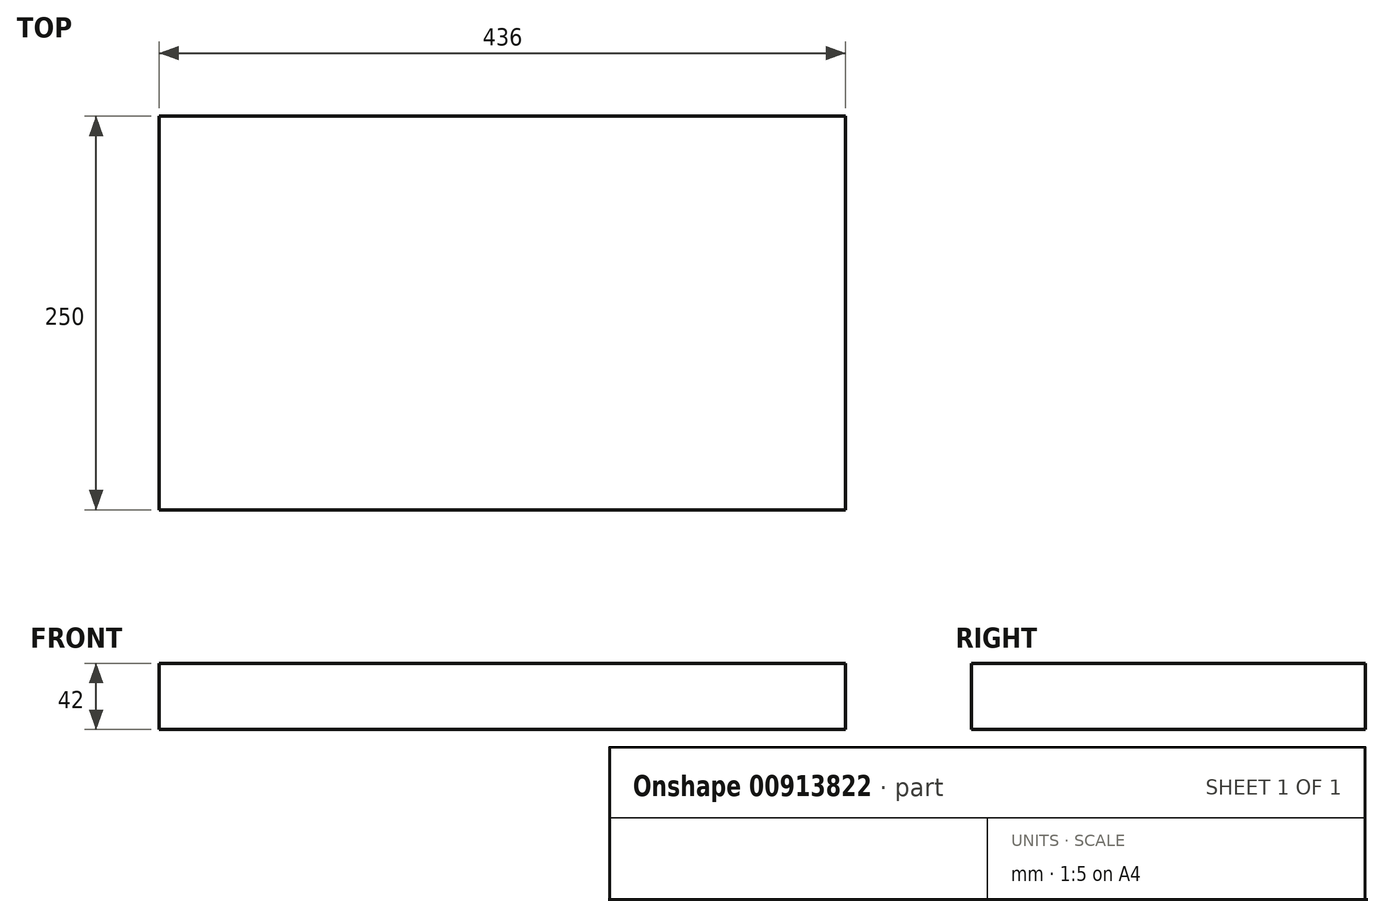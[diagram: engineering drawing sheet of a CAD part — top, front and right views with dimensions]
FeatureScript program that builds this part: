
annotation { "Feature Type Name" : "Feature", "Feature Type Description" : "" }
export const myFeature = defineFeature(function(context is Context, id is Id, definition is map)
    precondition{}
    {
        {
            var Q0;
            Q0=qCreatedBy(makeId("Top.planeOp"),FACE);
            var sketch = newSketch(context, id + "F0", { "sketchPlane" : qUnion([Q0])});
            skLineSegment(sketch, "E0.bottom", {"start": v(218, -125) * mm, "end": v(-218, -125) * mm});
            skLineSegment(sketch, "E0.top", {"start": v(218, 125) * mm, "end": v(-218, 125) * mm});
            skLineSegment(sketch, "E0.left", {"start": v(218, -125) * mm, "end": v(218, 125) * mm});
            skLineSegment(sketch, "E0.right", {"start": v(-218, -125) * mm, "end": v(-218, 125) * mm});
            skPoint(sketch, "E0.middle", {"position": v(0, 0) * mm});
            skSolve(sketch);
        }
        {
            var Q0;
            Q0=makeQuery(id+"F0.imprint","IMPRINT",FACE,{"disambiguationData":[TD([[makeQuery(id+"F0.imprint","IMPRINT",EDGE,{"derivedFrom":sQuery(id+"F0.wireOp",EDGE,"E0.bottom")}),-1.0]])]});
            extrude(context, id + "F1", {"entities" : qUnion([Q0]), "depth" : 42 * mm, "offsetDistance" : 25 * mm});
        }
    });
